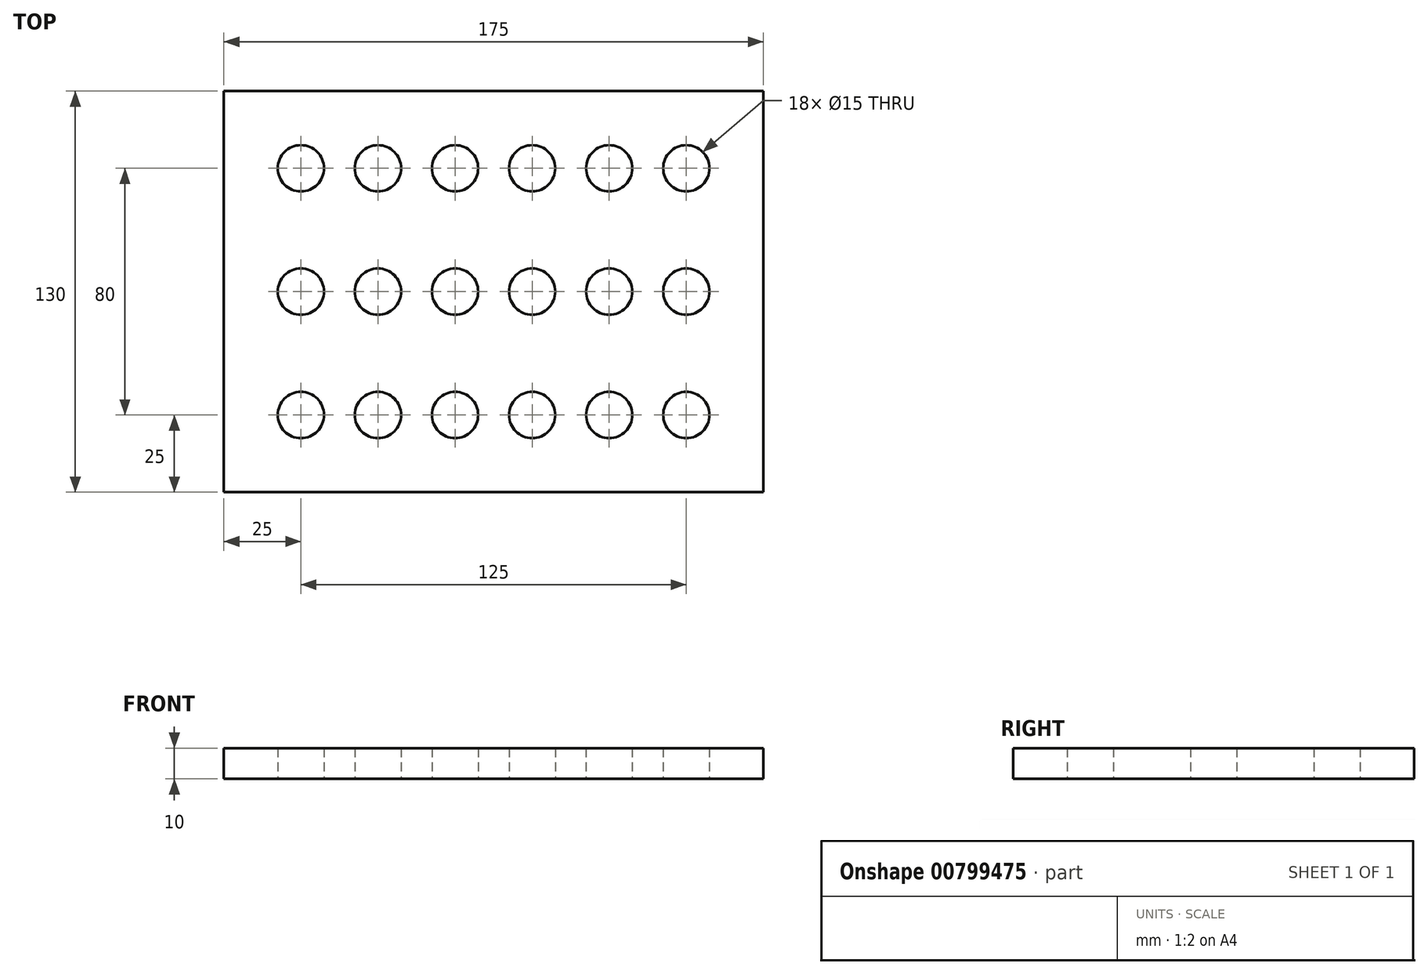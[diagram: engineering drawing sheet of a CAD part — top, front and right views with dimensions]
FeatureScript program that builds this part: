
annotation { "Feature Type Name" : "Feature", "Feature Type Description" : "" }
export const myFeature = defineFeature(function(context is Context, id is Id, definition is map)
    precondition{}
    {
        {
            var Q0;
            Q0=qCreatedBy(makeId("Top.planeOp"),FACE);
            var sketch = newSketch(context, id + "F0", { "sketchPlane" : qUnion([Q0])});
            skLineSegment(sketch, "E0.bottom", {"start": v(-87.5, 65) * mm, "end": v(87.5, 65) * mm});
            skLineSegment(sketch, "E0.top", {"start": v(-87.5, -65) * mm, "end": v(87.5, -65) * mm});
            skLineSegment(sketch, "E0.left", {"start": v(-87.5, 65) * mm, "end": v(-87.5, -65) * mm});
            skLineSegment(sketch, "E0.right", {"start": v(87.5, 65) * mm, "end": v(87.5, -65) * mm});
            skLineSegment(sketch, "E1", {"start": v(-87.5, 65) * mm, "end": v(87.5, -65) * mm, "construction": true});
            skLineSegment(sketch, "E2", {"start": v(-87.5, -65) * mm, "end": v(87.5, 65) * mm, "construction": true});
            skCircle(sketch, "E3", {"center": v(-62.5, 40) * mm, "radius": 7.5 * mm});
            skCircle(sketch, "E4.0.1.0", {"center": v(-62.5, 0) * mm, "radius": 7.5 * mm});
            skCircle(sketch, "E4.0.2.0", {"center": v(-62.5, -40) * mm, "radius": 7.5 * mm});
            skCircle(sketch, "E4.1.0.0", {"center": v(-37.5, 40) * mm, "radius": 7.5 * mm});
            skCircle(sketch, "E4.1.1.0", {"center": v(-37.5, 0) * mm, "radius": 7.5 * mm});
            skCircle(sketch, "E4.1.2.0", {"center": v(-37.5, -40) * mm, "radius": 7.5 * mm});
            skCircle(sketch, "E4.2.0.0", {"center": v(-12.5, 40) * mm, "radius": 7.5 * mm});
            skCircle(sketch, "E4.2.1.0", {"center": v(-12.5, 0) * mm, "radius": 7.5 * mm});
            skCircle(sketch, "E4.2.2.0", {"center": v(-12.5, -40) * mm, "radius": 7.5 * mm});
            skCircle(sketch, "E4.3.0.0", {"center": v(12.5, 40) * mm, "radius": 7.5 * mm});
            skCircle(sketch, "E4.3.1.0", {"center": v(12.5, 0) * mm, "radius": 7.5 * mm});
            skCircle(sketch, "E4.3.2.0", {"center": v(12.5, -40) * mm, "radius": 7.5 * mm});
            skCircle(sketch, "E4.4.0.0", {"center": v(37.5, 40) * mm, "radius": 7.5 * mm});
            skCircle(sketch, "E4.4.1.0", {"center": v(37.5, 0) * mm, "radius": 7.5 * mm});
            skCircle(sketch, "E4.4.2.0", {"center": v(37.5, -40) * mm, "radius": 7.5 * mm});
            skCircle(sketch, "E4.5.0.0", {"center": v(62.5, 40) * mm, "radius": 7.5 * mm});
            skCircle(sketch, "E4.5.1.0", {"center": v(62.5, 0) * mm, "radius": 7.5 * mm});
            skCircle(sketch, "E4.5.2.0", {"center": v(62.5, -40) * mm, "radius": 7.5 * mm});
            skLineSegment(sketch, "E4.direction1", {"start": v(-62.5, 40) * mm, "end": v(-37.5, 40) * mm, "construction": true});
            skLineSegment(sketch, "E4.direction2", {"start": v(-62.5, 40) * mm, "end": v(-62.5, 0) * mm, "construction": true});
            skSolve(sketch);
        }
        {
            var Q0;
            Q0 = qSketchRegion(id + "F0", true);
            extrude(context, id + "F1", {"entities" : qUnion([Q0]), "depth" : 10 * mm, "offsetDistance" : 25.4 * mm});
        }
    });
